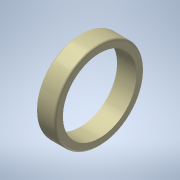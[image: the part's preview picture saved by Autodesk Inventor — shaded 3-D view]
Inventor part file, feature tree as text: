
AUTODESK INVENTOR PART (.ipt)
format: ipt  version: 2022.1 (Build 261234000, 234)  size: 128,512 bytes
history: native  units: mm
features: other x1, extrude x1, fillet x1, sketch x1
ambient origin geometry x8: Origin, YZ Plane, XZ Plane, XY Plane, X Axis, Y Axis, Z Axis, Center Point
bodies: Body1 (feature_tree)
feature tree (4):
  other  "Sólido1"
  extrude  "Extrusión1"  Depth=50.0mm TaperAngle=0.0deg
  fillet  "Empalme1"  Radius=5.0mm
  sketch  "Boceto1"  dims[d0=230.0mm d1=50.0mm d2=0.0mm d3=5.0mm d4=190.0mm]
